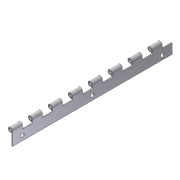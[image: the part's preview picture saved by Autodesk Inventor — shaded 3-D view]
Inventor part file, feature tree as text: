
AUTODESK INVENTOR PART (.ipt)
format: ipt  version: 2012 (Build 160160000, 160)  size: 162,304 bytes
history: native  units: in
note: dims shown in document units (in); Inventor stores cm internally (conversion verified against a paired STEP export)
features: extrude x3, sketch x3, fillet x1, pattern_linear x1, projected_geometry x1
ambient origin geometry x8: Origin, YZ Plane, XZ Plane, XY Plane, X Axis, Y Axis, Z Axis, Center Point
bodies: Solid1 (feature_tree)
feature tree (9):
  extrude  "Extrusion1"  Depth=0.09in
  extrude  "Extrusion2"  Depth=16.0in TaperAngle=0.0deg
  fillet  "Fillet1"  Radius=1.0in
  pattern_linear  "Rectangular Pattern1"  Spacing1=0.125in  [1 undecoded]
  extrude  "Extrusion3"  Depth=16.0in TaperAngle=0.0deg
  sketch  "Sketch1"  dims[d0=0.445in d1=0.09in]
  sketch  "Sketch2"  dims[d2=0.09in d3=16.0in d4=0.0in d5=1.0in]
  projected_geometry  "Projected Loop1"
  sketch  "Sketch3"  dims[d6=1.0in d7=0.125in d8=16.0in d9=0.0in d10=0.125in d11=3.1496in d13=2.0in d14=0.375in d15=1.0in d16=8.0in d17=1.0in d18=0.375in d19=0.375in d20=1.0in d21=0.0in]
note: 1 required parameter value undecoded (feature->parameter linkage not recoverable at this tier; creation-order binding heuristic only, values carry confidence <= 0.55)
